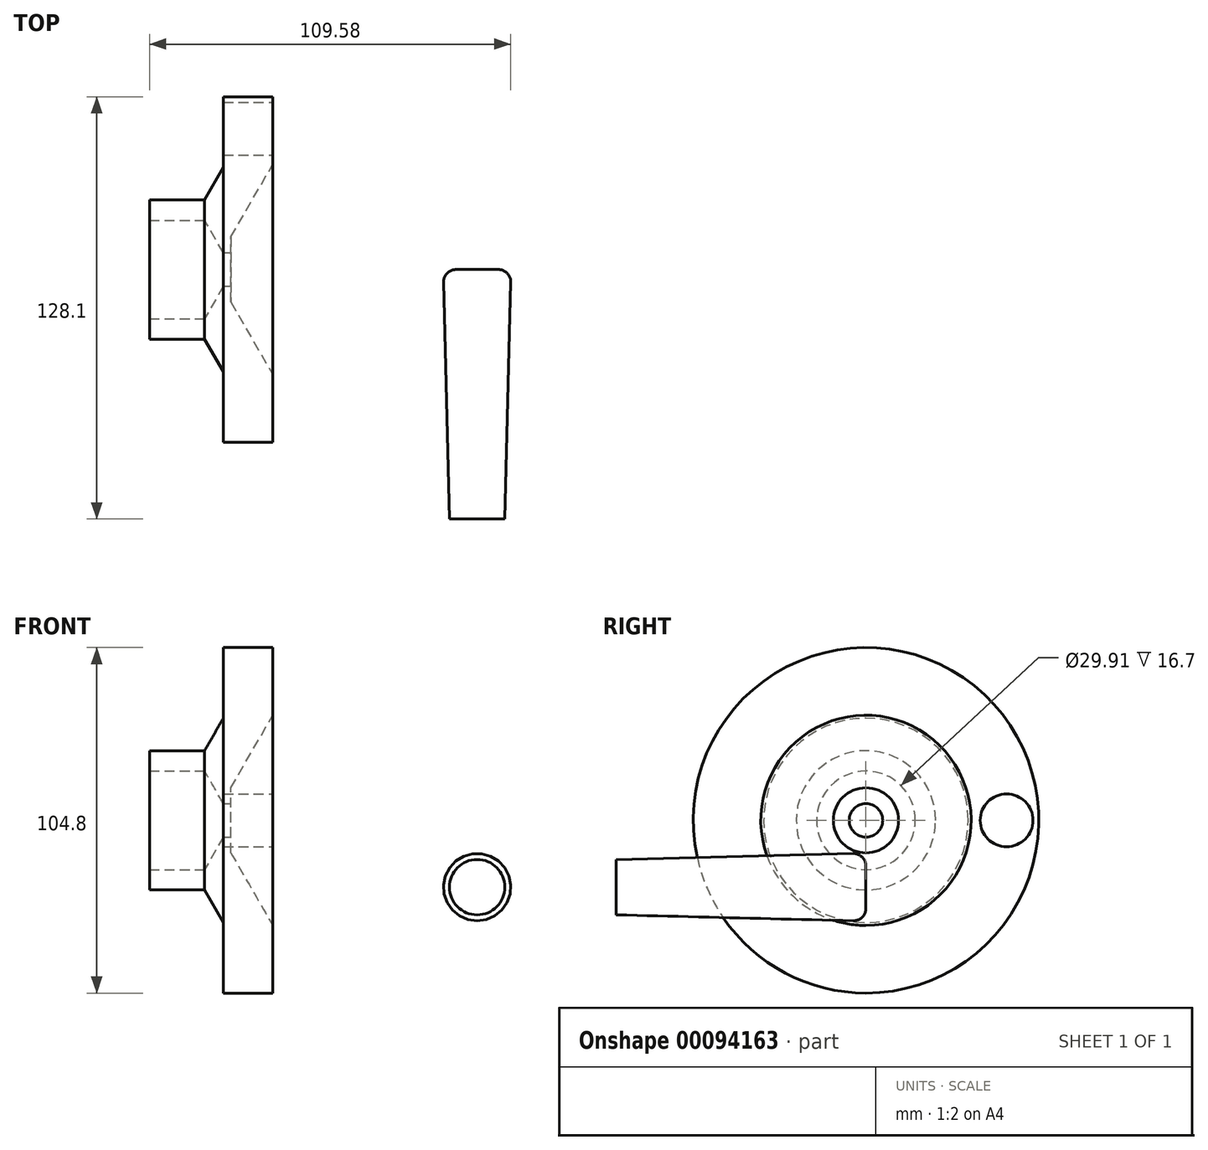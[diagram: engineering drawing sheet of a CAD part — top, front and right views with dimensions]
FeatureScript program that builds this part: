
annotation { "Feature Type Name" : "Feature", "Feature Type Description" : "" }
export const myFeature = defineFeature(function(context is Context, id is Id, definition is map)
    precondition{}
    {
        {
            var Q0;
            Q0=qCreatedBy(makeId("Right.planeOp"),FACE);
            var sketch = newSketch(context, id + "F0", { "sketchPlane" : qUnion([Q0])});
            skCircle(sketch, "E0", {"center": v(0, 0) * mm, "radius": 52.4 * mm});
            skCircle(sketch, "E1", {"center": v(42.66, 0) * mm, "radius": 8 * mm});
            skCircle(sketch, "E2", {"center": v(0, 0) * mm, "radius": 31.83 * mm});
            skSolve(sketch);
        }
        {
            var Q0;
            Q0=makeQuery(id+"F0.imprint","IMPRINT",FACE,{"disambiguationData":[TD([[makeQuery(id+"F0.imprint","IMPRINT",EDGE,{"derivedFrom":sQuery(id+"F0.wireOp",EDGE,"E0")}),1.0]])]});
            var Q1;
            Q1=makeQuery(id+"F0.imprint","IMPRINT",FACE,{"disambiguationData":[TD([[makeQuery(id+"F0.imprint","IMPRINT",EDGE,{"derivedFrom":sQuery(id+"F0.wireOp",EDGE,"E2")}),1.0]])]});
            extrude(context, id + "F1", {"entities" : qUnion([Q0, Q1]), "oppositeDirection" : true, "depth" : 15 * mm});
        }
        {
            var Q0;
            Q0=makeQuery(id+"F1.opExtrude","CAP_FACE",FACE,{"disambiguationData":[OSD([sQuery(id+"F0.wireOp",EDGE,"E0"),sQuery(id+"F0.wireOp",EDGE,"E1")])],"isStart":true});
            var sketch = newSketch(context, id + "F2", { "sketchPlane" : qUnion([Q0])});
            skCircle(sketch, "E3", {"center": v(0, 0) * mm, "radius": 31.88 * mm});
            skSolve(sketch);
        }
        {
            var Q0;
            Q0=makeQuery(id+"F2.imprint","IMPRINT",FACE,{"disambiguationData":[TD([[makeQuery(id+"F2.imprint","IMPRINT",EDGE,{"derivedFrom":sQuery(id+"F2.wireOp",EDGE,"E3")}),1.0]])]});
            extrude(context, id + "F3", {"entities" : qUnion([Q0]), "operationType" : NewBodyOperationType.REMOVE, "oppositeDirection" : true, "depth" : 12.7 * mm, "hasDraft" : true, "draftAngle" : 60 * degree, "draftPullDirection" : true});
        }
        {
            var Q0;
            Q0=makeQuery(id+"F3.boolean.opBoolean","COPY",FACE,{"derivedFrom":makeQuery(id+"F3.opExtrude","CAP_FACE",FACE,{"disambiguationData":[OSD([sQuery(id+"F2.wireOp",EDGE,"E3")])],"isStart":false})});
            var sketch = newSketch(context, id + "F4", { "sketchPlane" : qUnion([Q0])});
            skCircle(sketch, "E4", {"center": v(0, 0) * mm, "radius": 5.08 * mm});
            skSolve(sketch);
        }
        {
            var Q0;
            Q0=makeQuery(id+"F4.imprint","IMPRINT",FACE,{"disambiguationData":[TD([[makeQuery(id+"F4.imprint","IMPRINT",EDGE,{"derivedFrom":sQuery(id+"F4.wireOp",EDGE,"E4")}),1.0]])]});
            extrude(context, id + "F5", {"entities" : qUnion([Q0]), "operationType" : NewBodyOperationType.REMOVE, "endBound" : BoundingType.THROUGH_ALL, "oppositeDirection" : true, "depth" : 25.4 * mm});
        }
        {
            var Q0;
            Q0=makeQuery(id+"F1.opExtrude","CAP_FACE",FACE,{"disambiguationData":[OSD([sQuery(id+"F0.wireOp",EDGE,"E0"),sQuery(id+"F0.wireOp",EDGE,"E1")])],"isStart":false});
            var sketch = newSketch(context, id + "F6", { "sketchPlane" : qUnion([Q0])});
            skCircle(sketch, "E5", {"center": v(0, 0) * mm, "radius": 31 * mm});
            skSolve(sketch);
        }
        {
            var Q0;
            Q0=makeQuery(id+"F6.imprint","IMPRINT",FACE,{"disambiguationData":[TD([[makeQuery(id+"F6.imprint","IMPRINT",EDGE,{"derivedFrom":sQuery(id+"F6.wireOp",EDGE,"E5")}),1.0]])]});
            extrude(context, id + "F7", {"entities" : qUnion([Q0]), "operationType" : NewBodyOperationType.ADD, "depth" : 5.7 * mm, "hasDraft" : true, "draftAngle" : 60 * degree, "draftPullDirection" : true});
        }
        {
            var Q0;
            Q0=makeQuery(id+"F7.opExtrude","CAP_FACE",FACE,{"disambiguationData":[OSD([sQuery(id+"F0.wireOp",EDGE,"E0"),sQuery(id+"F0.wireOp",EDGE,"E1"),sQuery(id+"F4.wireOp",EDGE,"E4"),sQuery(id+"F6.wireOp",EDGE,"E5")])],"isStart":false});
            extrude(context, id + "F8", {"entities" : qUnion([Q0]), "operationType" : NewBodyOperationType.ADD, "depth" : 16.7 * mm});
        }
        {
            var Q0;
            Q0=qCreatedBy(makeId("Front.planeOp"),FACE);
            var sketch = newSketch(context, id + "F9", { "sketchPlane" : qUnion([Q0])});
            skCircle(sketch, "E6", {"center": v(61.98, -20.27) * mm, "radius": 10.3 * mm});
            skSolve(sketch);
        }
        {
            var Q0;
            Q0=makeQuery(id+"F9.imprint","IMPRINT",FACE,{"disambiguationData":[TD([[makeQuery(id+"F9.imprint","IMPRINT",EDGE,{"derivedFrom":sQuery(id+"F9.wireOp",EDGE,"E6")}),1.0]])]});
            extrude(context, id + "F10", {"entities" : qUnion([Q0]), "depth" : 75.7 * mm, "hasDraft" : true, "draftAngle" : 1.44 * degree, "draftPullDirection" : true});
        }
        {
            var Q0;
            Q0=makeQuery(id+"F10.opExtrude","CAP_EDGE",EDGE,{"disambiguationData":[OSD([sQuery(id+"F9.wireOp",EDGE,"E6")])],"isStart":true});
            fillet(context, id + "F11", {"entities" : qUnion([Q0]), "radius" : 3.8 * mm, "tangentPropagation" : true, "allowEdgeOverflow" : false});
        }
    });
